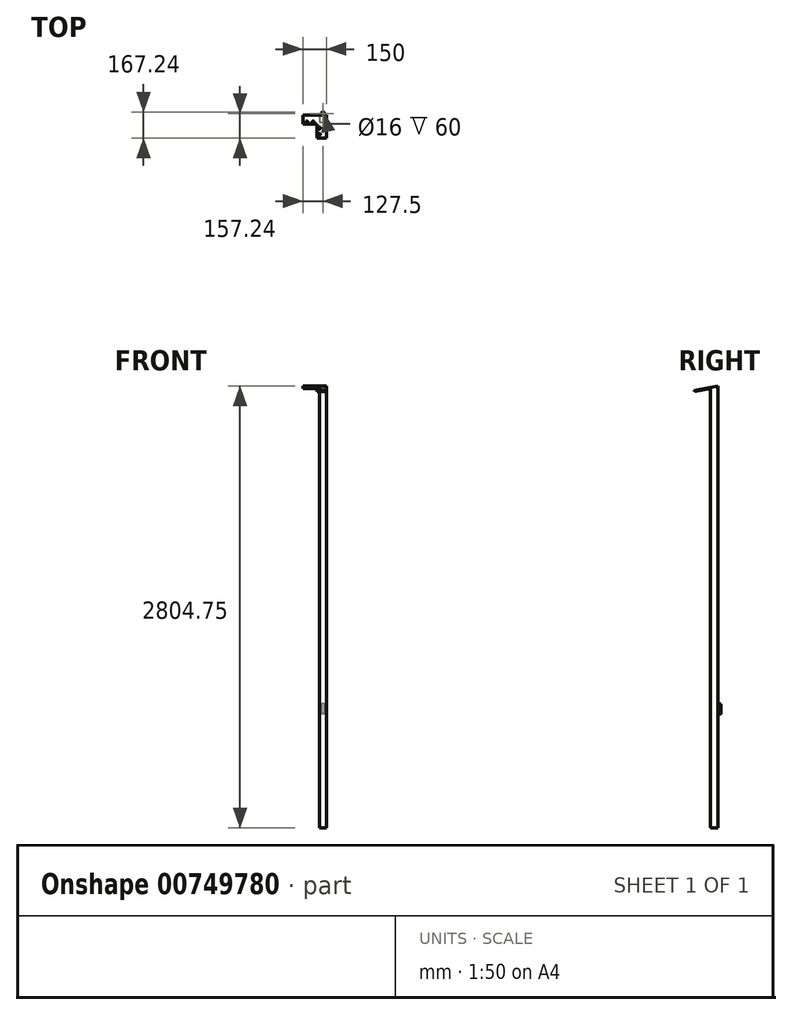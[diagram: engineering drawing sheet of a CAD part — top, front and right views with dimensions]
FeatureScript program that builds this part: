
annotation { "Feature Type Name" : "Feature", "Feature Type Description" : "" }
export const myFeature = defineFeature(function(context is Context, id is Id, definition is map)
    precondition{}
    {
        {
            var Q0;
            Q0=qCreatedBy(makeId("Top.planeOp"),FACE);
            var sketch = newSketch(context, id + "F0", { "sketchPlane" : qUnion([Q0])});
            skLineSegment(sketch, "E0.bottom", {"start": v(22.5, -22.5) * mm, "end": v(-22.5, -22.5) * mm});
            skLineSegment(sketch, "E0.top", {"start": v(22.5, 22.5) * mm, "end": v(-22.5, 22.5) * mm});
            skLineSegment(sketch, "E0.left", {"start": v(22.5, -22.5) * mm, "end": v(22.5, 22.5) * mm});
            skLineSegment(sketch, "E0.right", {"start": v(-22.5, -22.5) * mm, "end": v(-22.5, 22.5) * mm});
            skPoint(sketch, "E0.middle", {"position": v(0, 0) * mm});
            skSolve(sketch);
        }
        {
            var Q0;
            Q0=qSketchRegion(id+"F0",true);
            extrude(context, id + "F1", {"entities" : qUnion([Q0]), "depth" : 3330 * mm, "offsetDistance" : 25 * mm});
        }
        {
            var Q0;
            Q0=qCreatedBy(makeId("Top.planeOp"),FACE);
            cPlane(context, id + "F2", {"entities" : qUnion([Q0]), "cplaneType" : CPlaneType.OFFSET, "offset" : 1256 * mm, "width" : 150 * mm, "height" : 150 * mm});
        }
        {
            var Q0;
            Q0=qCreatedBy(id+"F2.planeOp",FACE);
            var sketch = newSketch(context, id + "F3", { "sketchPlane" : qUnion([Q0])});
            skLineSegment(sketch, "E1", {"start": v(0, 0) * mm, "end": v(22.5, 0) * mm});
            skLineSegment(sketch, "E2", {"start": v(0, 0) * mm, "end": v(-22.5, 0) * mm});
            skLineSegment(sketch, "E3", {"start": v(0, 0) * mm, "end": v(0, 22.5) * mm});
            skLineSegment(sketch, "E4", {"start": v(0, 22.5) * mm, "end": v(0, 32.5) * mm});
            skCircle(sketch, "E5", {"center": v(0, 32.5) * mm, "radius": 10 * mm});
            skLineSegment(sketch, "E6.bottom", {"start": v(10, 22.5) * mm, "end": v(-10, 22.5) * mm});
            skLineSegment(sketch, "E6.left", {"start": v(10, 22.5) * mm, "end": v(10, 32.5) * mm});
            skLineSegment(sketch, "E6.right", {"start": v(-10, 22.5) * mm, "end": v(-10, 32.5) * mm});
            skSolve(sketch);
        }
        {
            var Q0;
            Q0=makeQuery(id+"F1.opExtrude","CAP_EDGE",EDGE,{"disambiguationData":[OSD([sQuery(id+"F0.wireOp",EDGE,"E0.bottom")])],"isStart":false});
            cPlane(context, id + "F4", {"entities" : qUnion([Q0]), "cplaneType" : CPlaneType.LINE_ANGLE, "offset" : 25 * mm, "angle" : 101 * degree, "oppositeDirection" : true, "width" : 150 * mm, "height" : 150 * mm});
        }
        {
            var Q0;
            Q0=makeQuery(id+"F1.opExtrude","CAP_FACE",FACE,{"disambiguationData":[OSD([sQuery(id+"F0.wireOp",EDGE,"E0.bottom"),sQuery(id+"F0.wireOp",EDGE,"E0.top"),sQuery(id+"F0.wireOp",EDGE,"E0.left"),sQuery(id+"F0.wireOp",EDGE,"E0.right")])],"isStart":false});
            var sketch = newSketch(context, id + "F5", { "sketchPlane" : qUnion([Q0])});
            skLineSegment(sketch, "E7.bottom", {"start": v(-22.5, 22.5) * mm, "end": v(22.5, 22.5) * mm});
            skLineSegment(sketch, "E7.top", {"start": v(-22.5, -22.5) * mm, "end": v(22.5, -22.5) * mm});
            skLineSegment(sketch, "E7.left", {"start": v(-22.5, 22.5) * mm, "end": v(-22.5, -22.5) * mm});
            skLineSegment(sketch, "E7.right", {"start": v(22.5, 22.5) * mm, "end": v(22.5, -22.5) * mm});
            skSolve(sketch);
        }
        {
            var Q0;
            Q0=qCreatedBy(id+"F4.planeOp",FACE);
            var sketch = newSketch(context, id + "F6", { "sketchPlane" : qUnion([Q0])});
            skLineSegment(sketch, "E8.bottom", {"start": v(-22.5, -659.15) * mm, "end": v(22.5, -659.15) * mm});
            skLineSegment(sketch, "E8.top", {"start": v(-22.5, -613.3) * mm, "end": v(22.5, -613.3) * mm});
            skLineSegment(sketch, "E8.left", {"start": v(-22.5, -659.15) * mm, "end": v(-22.5, -613.3) * mm});
            skLineSegment(sketch, "E8.right", {"start": v(22.5, -659.15) * mm, "end": v(22.5, -613.3) * mm});
            skSolve(sketch);
        }
        {
            var Q0;
            Q0=makeQuery(id+"F6.imprint","IMPRINT",FACE,{"disambiguationData":[TD([[makeQuery(id+"F6.imprint","IMPRINT",EDGE,{"derivedFrom":sQuery(id+"F6.wireOp",EDGE,"E8.bottom")}),1.0]])]});
            extrude(context, id + "F7", {"entities" : qUnion([Q0]), "operationType" : NewBodyOperationType.ADD, "depth" : 25 * mm, "offsetDistance" : 25 * mm});
        }
        {
            var Q0;
            Q0=qCreatedBy(id+"F4.planeOp",FACE);
            var sketch = newSketch(context, id + "F8", { "sketchPlane" : qUnion([Q0])});
            skLineSegment(sketch, "E9.bottom", {"start": v(22.5, -659.15) * mm, "end": v(-127.5, -659.15) * mm});
            skLineSegment(sketch, "E9.top", {"start": v(22.5, -599.15) * mm, "end": v(-127.5, -599.15) * mm});
            skLineSegment(sketch, "E9.left", {"start": v(22.5, -659.15) * mm, "end": v(22.5, -599.15) * mm});
            skLineSegment(sketch, "E9.right", {"start": v(-127.5, -659.15) * mm, "end": v(-127.5, -599.15) * mm});
            skLineSegment(sketch, "E10", {"start": v(22.5, -659.15) * mm, "end": v(-37.5, -659.15) * mm});
            skLineSegment(sketch, "E11.bottom", {"start": v(-37.5, -659.15) * mm, "end": v(22.5, -659.15) * mm});
            skLineSegment(sketch, "E11.top", {"start": v(-37.5, -509.15) * mm, "end": v(22.5, -509.15) * mm});
            skLineSegment(sketch, "E11.left", {"start": v(-37.5, -659.15) * mm, "end": v(-37.5, -509.15) * mm});
            skLineSegment(sketch, "E11.right", {"start": v(22.5, -659.15) * mm, "end": v(22.5, -509.15) * mm});
            skSolve(sketch);
        }
        {
            var Q0;
            Q0=qSketchRegion(id+"F8",true);
            extrude(context, id + "F9", {"entities" : qUnion([Q0]), "operationType" : NewBodyOperationType.ADD, "depth" : 5 * mm, "offsetDistance" : 25 * mm});
        }
        {
            var Q0;
            Q0=makeQuery(id+"F9.boolean.opBoolean","MERGE",FACE,{"derivedFrom":[makeQuery(id+"F7.opExtrude","CAP_FACE",FACE,{"disambiguationData":[OSD([sQuery(id+"F6.wireOp",EDGE,"E8.bottom"),sQuery(id+"F6.wireOp",EDGE,"E8.top"),sQuery(id+"F6.wireOp",EDGE,"E8.left"),sQuery(id+"F6.wireOp",EDGE,"E8.right")])],"isStart":true}),makeQuery(id+"F9.opExtrude","CAP_FACE",FACE,{"disambiguationData":[OSD([sQuery(id+"F8.wireOp",EDGE,"8cb1c19a-3ec8-4bcf-bfa4-e708c15dc5ac.bottom"),sQuery(id+"F8.wireOp",EDGE,"74325b9e-44c1-4043-a874-969d41da8b4c.bottom"),sQuery(id+"F8.wireOp",EDGE,"74325b9e-44c1-4043-a874-969d41da8b4c.top"),sQuery(id+"F8.wireOp",EDGE,"74325b9e-44c1-4043-a874-969d41da8b4c.right"),sQuery(id+"F8.wireOp",EDGE,"880eba7a-782f-4c27-b6fe-715e12f068d6.top"),sQuery(id+"F8.wireOp",EDGE,"880eba7a-782f-4c27-b6fe-715e12f068d6.right"),sQuery(id+"F8.wireOp",EDGE,"59256244-9167-4ee1-a51c-4aa0c58c6036")])],"isStart":true})]});
            var sketch = newSketch(context, id + "F10", { "sketchPlane" : qUnion([Q0])});
            skLineSegment(sketch, "E12", {"start": v(-22.5, 471.42) * mm, "end": v(22.5, 471.42) * mm});
            skLineSegment(sketch, "E13", {"start": v(0, 471.42) * mm, "end": v(0, 519.36) * mm});
            skCircle(sketch, "E14.MirrorC", {"center": v(-22.5, 534.15) * mm, "radius": 6 * mm});
            skCircle(sketch, "E15.MirrorC", {"center": v(-22.5, 574.15) * mm, "radius": 6 * mm});
            skCircle(sketch, "E16.MirrorC", {"center": v(-62.5, 614.15) * mm, "radius": 6 * mm});
            skCircle(sketch, "E17.MirrorC", {"center": v(-102.5, 614.15) * mm, "radius": 6 * mm});
            skSolve(sketch);
        }
        {
            var Q0;
            Q0=qSketchRegion(id+"F10",true);
            extrude(context, id + "F11", {"entities" : qUnion([Q0]), "operationType" : NewBodyOperationType.REMOVE, "oppositeDirection" : true, "depth" : 25 * mm, "offsetDistance" : 25 * mm});
        }
        {
            var Q0;
            Q0=qCreatedBy(makeId("Top.planeOp"),FACE);
            var sketch = newSketch(context, id + "F12", { "sketchPlane" : qUnion([Q0])});
            skLineSegment(sketch, "E18.bottom", {"start": v(-22.5, 22.5) * mm, "end": v(127.5, 22.5) * mm});
            skLineSegment(sketch, "E18.top", {"start": v(-22.5, 27.27) * mm, "end": v(127.5, 27.27) * mm});
            skLineSegment(sketch, "E18.left", {"start": v(-22.5, 22.5) * mm, "end": v(-22.5, 27.27) * mm});
            skLineSegment(sketch, "E18.right", {"start": v(127.5, 22.5) * mm, "end": v(127.5, 27.27) * mm});
            skSolve(sketch);
        }
        {
            var Q0;
            Q0 = qSketchRegion(id + "F3", true);
            extrude(context, id + "F13", {"entities" : qUnion([Q0]), "operationType" : NewBodyOperationType.ADD, "depth" : 5 * mm, "offsetDistance" : 25 * mm});
        }
        {
            var Q0;
            Q0=makeQuery(id+"F13.opExtrude","CAP_FACE",FACE,{"disambiguationData":[OSD([sQuery(id+"F3.wireOp",EDGE,"E5")])],"isStart":false});
            var sketch = newSketch(context, id + "F14", { "sketchPlane" : qUnion([Q0])});
            skCircle(sketch, "E19", {"center": v(0, 32.5) * mm, "radius": 10 * mm});
            skCircle(sketch, "E20", {"center": v(0, 32.5) * mm, "radius": 8 * mm});
            skLineSegment(sketch, "E21.0", {"start": v(10, 22.5) * mm, "end": v(10, 32.5) * mm});
            skLineSegment(sketch, "E22.0", {"start": v(10, 22.5) * mm, "end": v(-10, 22.5) * mm});
            skPoint(sketch, "E23.0", {"position": v(-10, 22.5) * mm});
            skLineSegment(sketch, "E24.0", {"start": v(-10, 22.5) * mm, "end": v(-10, 32.5) * mm});
            skSolve(sketch);
        }
        {
            var Q0;
            Q0 = qSketchRegion(id + "F14", true);
            extrude(context, id + "F15", {"entities" : qUnion([Q0]), "operationType" : NewBodyOperationType.ADD, "depth" : 60 * mm, "offsetDistance" : 25 * mm});
        }
        {
            var Q0;
            Q0=makeQuery(id+"F1.opExtrude","CAP_FACE",FACE,{"disambiguationData":[OSD([sQuery(id+"F0.wireOp",EDGE,"E0.bottom"),sQuery(id+"F0.wireOp",EDGE,"E0.top"),sQuery(id+"F0.wireOp",EDGE,"E0.left"),sQuery(id+"F0.wireOp",EDGE,"E0.right")])],"isStart":true});
            var sketch = newSketch(context, id + "F16", { "sketchPlane" : qUnion([Q0])});
            skLineSegment(sketch, "E25.bottom", {"start": v(-22.5, 22.5) * mm, "end": v(22.5, 22.5) * mm});
            skLineSegment(sketch, "E25.top", {"start": v(-22.5, -22.5) * mm, "end": v(22.5, -22.5) * mm});
            skLineSegment(sketch, "E25.left", {"start": v(-22.5, 22.5) * mm, "end": v(-22.5, -22.5) * mm});
            skLineSegment(sketch, "E25.right", {"start": v(22.5, 22.5) * mm, "end": v(22.5, -22.5) * mm});
            skSolve(sketch);
        }
        {
            var Q0;
            Q0 = qSketchRegion(id + "F16", true);
            extrude(context, id + "F17", {"entities" : qUnion([Q0]), "operationType" : NewBodyOperationType.REMOVE, "oppositeDirection" : true, "depth" : 534 * mm, "offsetDistance" : 25 * mm});
        }
        {
            var Q0;
            Q0=makeQuery(id+"F9.boolean.opBoolean","MERGE",FACE,{"derivedFrom":[makeQuery(id+"F7.boolean.opBoolean","MERGE",FACE,{"derivedFrom":[makeQuery(id+"F1.opExtrude","SWEPT_FACE",FACE,{"disambiguationData":[OSD([sQuery(id+"F0.wireOp",EDGE,"E0.left")])]}),makeQuery(id+"F7.opExtrude","SWEPT_FACE",FACE,{"disambiguationData":[OSD([sQuery(id+"F6.wireOp",EDGE,"E8.right")])]})]}),makeQuery(id+"F9.opExtrude","SWEPT_FACE",FACE,{"disambiguationData":[OSD([sQuery(id+"F8.wireOp",EDGE,"E11.right")])]})]});
            var sketch = newSketch(context, id + "F18", { "sketchPlane" : qUnion([Q0])});
            skLineSegment(sketch, "E26", {"start": v(22.5, 3313.28) * mm, "end": v(22.5, 3338.75) * mm});
            skLineSegment(sketch, "E27", {"start": v(22.5, 3338.75) * mm, "end": v(27.27, 3314.2) * mm});
            skLineSegment(sketch, "E28", {"start": v(27.27, 3314.2) * mm, "end": v(22.5, 3313.28) * mm});
            skSolve(sketch);
        }
        {
            var Q0;
            Q0 = qSketchRegion(id + "F18", true);
            extrude(context, id + "F19", {"entities" : qUnion([Q0]), "operationType" : NewBodyOperationType.REMOVE, "endBound" : BoundingType.UP_TO_NEXT, "oppositeDirection" : true, "depth" : 25 * mm, "offsetDistance" : 25 * mm});
        }
    });
